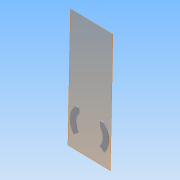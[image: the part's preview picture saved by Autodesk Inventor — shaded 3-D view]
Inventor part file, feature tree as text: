
AUTODESK INVENTOR PART (.ipt)
format: ipt  version: 2013 (Build 170138000, 138)  size: 100,352 bytes
history: native  units: in
note: dims shown in document units (in); Inventor stores cm internally (conversion verified against a paired STEP export)
features: extrude x2, plane x1, other x1, reference x1
ambient origin geometry x8: Origin, YZ Plane, XZ Plane, XY Plane, X Axis, Y Axis, Z Axis, Center Point
bodies: Solid1 (feature_tree)
feature tree (5):
  plane  "Work Plane1"
  other  "ThermoBulbBorder"
  extrude  "Sides"  Depth=24.0in
  extrude  "Extrusion2"  Depth=0.71in TaperAngle=0.0deg
  reference  "Reference2"
